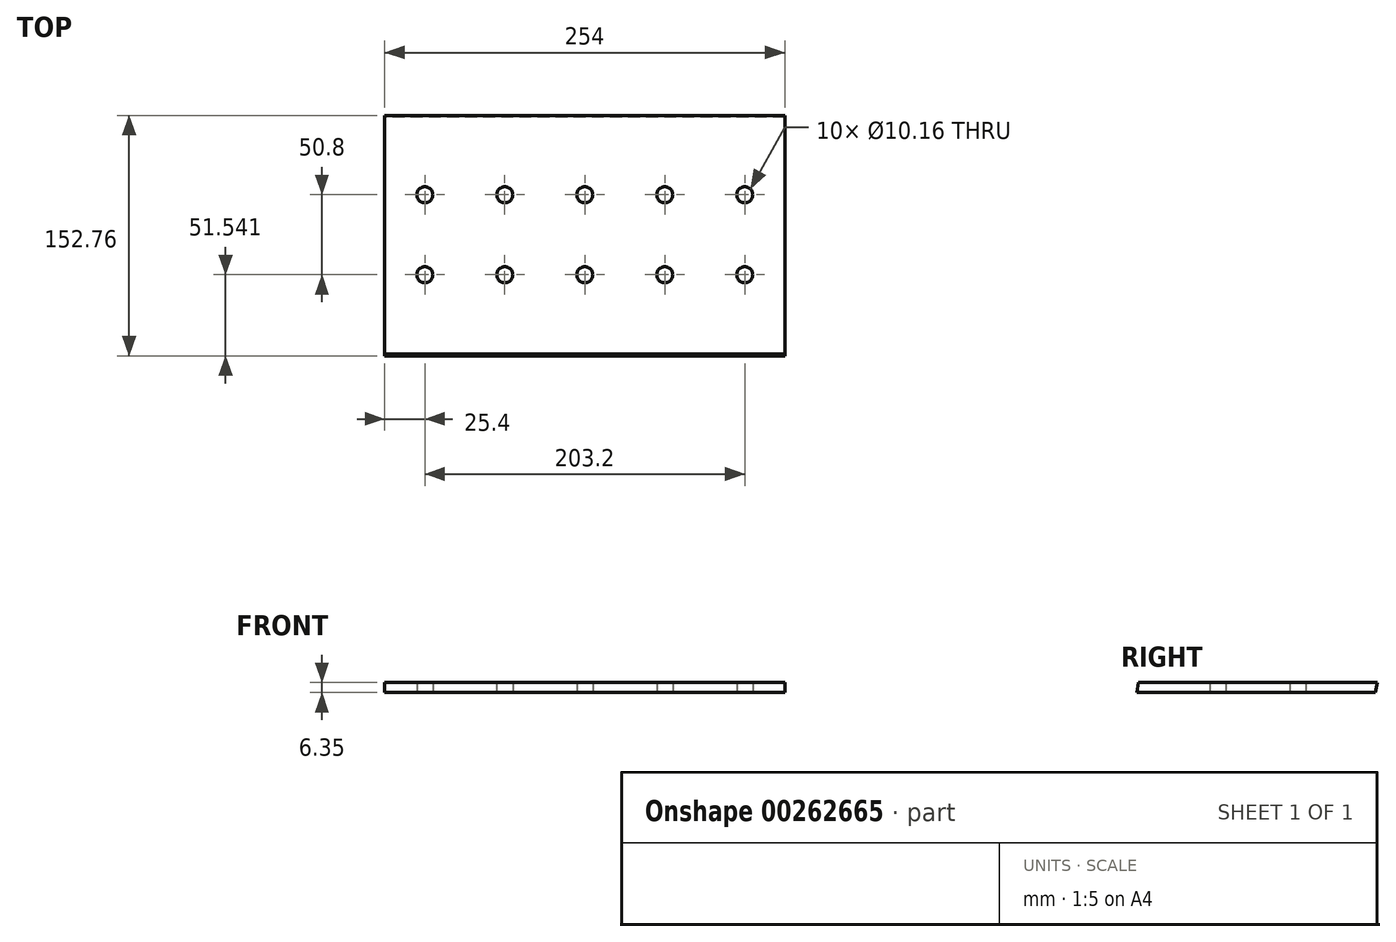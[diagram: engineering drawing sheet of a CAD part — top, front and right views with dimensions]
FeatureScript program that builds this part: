
annotation { "Feature Type Name" : "Feature", "Feature Type Description" : "" }
export const myFeature = defineFeature(function(context is Context, id is Id, definition is map)
    precondition{}
    {
        {
            var Q0;
            Q0=qCreatedBy(makeId("Top.planeOp"),FACE);
            var sketch = newSketch(context, id + "F0", { "sketchPlane" : qUnion([Q0])});
            skLineSegment(sketch, "E0.bottom", {"start": v(0, 0) * mm, "end": v(254, 0) * mm});
            skLineSegment(sketch, "E0.top", {"start": v(0, 165.1) * mm, "end": v(254, 165.1) * mm});
            skLineSegment(sketch, "E0.left", {"start": v(0, 0) * mm, "end": v(0, 165.1) * mm});
            skLineSegment(sketch, "E0.right", {"start": v(254, 0) * mm, "end": v(254, 165.1) * mm});
            skCircle(sketch, "E1", {"center": v(25.4, 63.88) * mm, "radius": 5.08 * mm});
            skCircle(sketch, "E2.0.1.0", {"center": v(25.4, 114.68) * mm, "radius": 5.08 * mm});
            skCircle(sketch, "E2.1.0.0", {"center": v(76.2, 63.88) * mm, "radius": 5.08 * mm});
            skCircle(sketch, "E2.1.1.0", {"center": v(76.2, 114.68) * mm, "radius": 5.08 * mm});
            skCircle(sketch, "E2.2.0.0", {"center": v(127, 63.88) * mm, "radius": 5.08 * mm});
            skCircle(sketch, "E2.2.1.0", {"center": v(127, 114.68) * mm, "radius": 5.08 * mm});
            skCircle(sketch, "E2.3.0.0", {"center": v(177.8, 63.88) * mm, "radius": 5.08 * mm});
            skCircle(sketch, "E2.3.1.0", {"center": v(177.8, 114.68) * mm, "radius": 5.08 * mm});
            skCircle(sketch, "E2.4.0.0", {"center": v(228.6, 63.88) * mm, "radius": 5.08 * mm});
            skCircle(sketch, "E2.4.1.0", {"center": v(228.6, 114.68) * mm, "radius": 5.08 * mm});
            skLineSegment(sketch, "E2.direction1", {"start": v(25.4, 63.88) * mm, "end": v(76.2, 63.88) * mm, "construction": true});
            skLineSegment(sketch, "E2.direction2", {"start": v(25.4, 63.88) * mm, "end": v(25.4, 114.68) * mm, "construction": true});
            skSolve(sketch);
        }
        {
            var Q0;
            Q0=makeQuery(id+"F0.imprint","IMPRINT",FACE,{"disambiguationData":[TD([[makeQuery(id+"F0.imprint","IMPRINT",EDGE,{"derivedFrom":sQuery(id+"F0.wireOp",EDGE,"E0.bottom")}),1.0]])]});
            extrude(context, id + "F1", {"entities" : qUnion([Q0]), "depth" : 6.35 * mm});
        }
        {
            var Q0;
            Q0=makeQuery(id+"F1.opExtrude","SWEPT_FACE",FACE,{"disambiguationData":[OSD([sQuery(id+"F0.wireOp",EDGE,"E0.left")])]});
            var sketch = newSketch(context, id + "F2", { "sketchPlane" : qUnion([Q0])});
            skLineSegment(sketch, "E3", {"start": v(-165.1, 6.35) * mm, "end": v(-161.95, -11.5) * mm});
            skLineSegment(sketch, "E4", {"start": v(-165.1, 6.35) * mm, "end": v(-165.1, -11.5) * mm});
            skLineSegment(sketch, "E5", {"start": v(-165.1, -11.5) * mm, "end": v(-161.95, -11.5) * mm});
            skSolve(sketch);
        }
        {
            var Q0;
            {var subQ0=sQuery(id+"F2.wireOp",EDGE,"E4");var subQ2=sQuery(id+"F0.wireOp",EDGE,"E0.left");var subQ4=makeQuery(id+"F1.opExtrude","CAP_EDGE",EDGE,{"disambiguationData":[OSD([subQ2])],"isStart":true});var subQ6=makeQuery(id+"F2.imprint","INTERSECT",VERTEX,{"derivedFrom":[subQ4,subQ0]});Q0=makeQuery(id+"F2.imprint","IMPRINT",FACE,{"disambiguationData":[TD([[makeQuery(id+"F2.imprint","IMPRINT",EDGE,{"disambiguationData":[TD([[subQ6,1.0]])],"derivedFrom":subQ4}),-1.0]])]});}
            extrude(context, id + "F3", {"entities" : qUnion([Q0]), "operationType" : NewBodyOperationType.REMOVE, "endBound" : BoundingType.THROUGH_ALL, "oppositeDirection" : true, "depth" : 25.4 * mm});
        }
        {
            var Q0;
            Q0=makeQuery(id+"F1.opExtrude","SWEPT_FACE",FACE,{"disambiguationData":[OSD([sQuery(id+"F0.wireOp",EDGE,"E0.left")])]});
            var sketch = newSketch(context, id + "F4", { "sketchPlane" : qUnion([Q0])});
            skLineSegment(sketch, "E6", {"start": v(-165.1, 6.35) * mm, "end": v(-13.46, 6.35) * mm});
            skLineSegment(sketch, "E7", {"start": v(-13.46, 6.35) * mm, "end": v(19.53, -180.78) * mm});
            skLineSegment(sketch, "E8", {"start": v(19.53, -180.78) * mm, "end": v(19.53, 6.35) * mm});
            skLineSegment(sketch, "E9", {"start": v(19.53, 6.35) * mm, "end": v(-13.46, 6.35) * mm});
            skSolve(sketch);
        }
        {
            var Q0;
            {var subQ3=sQuery(id+"F0.wireOp",EDGE,"E0.left");var subQ6=makeQuery(id+"F1.opExtrude","SWEPT_EDGE",EDGE,{"disambiguationData":[OSD([sQuery(id+"F0.wireOp",EDGE,"E0.bottom"),subQ3])]});Q0=makeQuery(id+"F4.imprint","IMPRINT",FACE,{"disambiguationData":[TD([[makeQuery(id+"F4.imprint","IMPRINT",EDGE,{"derivedFrom":subQ6}),-1.0]])]});}
            extrude(context, id + "F5", {"entities" : qUnion([Q0]), "operationType" : NewBodyOperationType.REMOVE, "endBound" : BoundingType.THROUGH_ALL, "oppositeDirection" : true, "depth" : 25.4 * mm});
        }
    });
